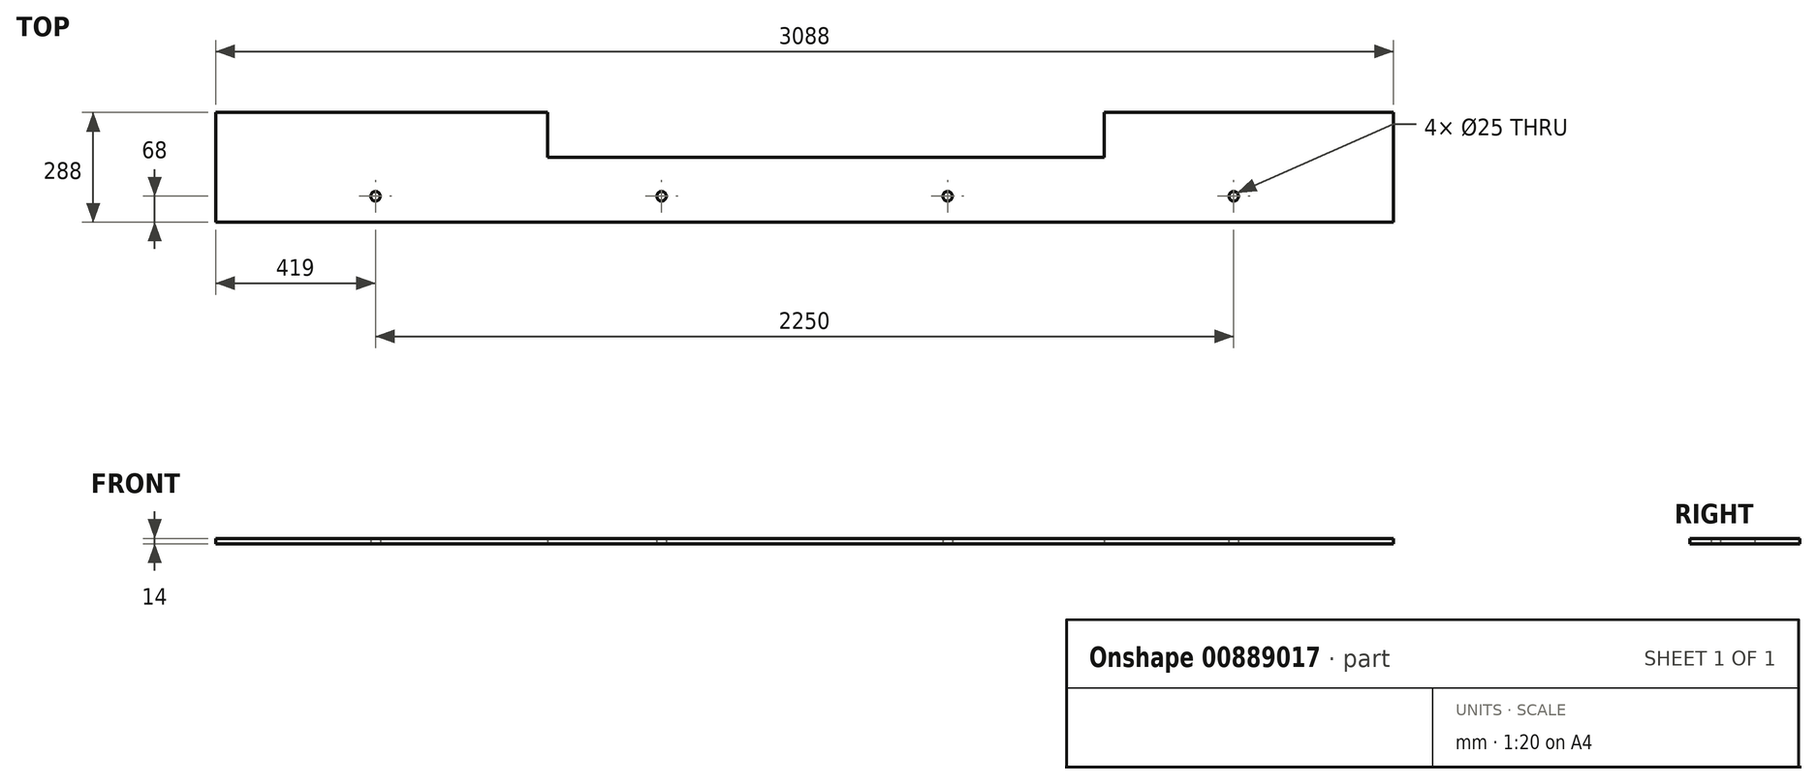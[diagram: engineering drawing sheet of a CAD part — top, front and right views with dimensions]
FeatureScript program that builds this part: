
annotation { "Feature Type Name" : "Feature", "Feature Type Description" : "" }
export const myFeature = defineFeature(function(context is Context, id is Id, definition is map)
    precondition{}
    {
        {
            var Q0;
            Q0=qCreatedBy(makeId("Top.planeOp"),FACE);
            var sketch = newSketch(context, id + "F0", { "sketchPlane" : qUnion([Q0])});
            skLineSegment(sketch, "E0.bottom", {"start": v(-1544, 144) * mm, "end": v(1544, 144) * mm});
            skLineSegment(sketch, "E0.top", {"start": v(-1544, -144) * mm, "end": v(1544, -144) * mm});
            skLineSegment(sketch, "E0.left", {"start": v(-1544, 144) * mm, "end": v(-1544, -144) * mm});
            skLineSegment(sketch, "E0.right", {"start": v(1544, 144) * mm, "end": v(1544, -144) * mm});
            skPoint(sketch, "E0.middle", {"position": v(0, 0) * mm});
            skSolve(sketch);
        }
        {
            var Q0;
            Q0=qSketchRegion(id+"F0",true);
            extrude(context, id + "F1", {"entities" : qUnion([Q0]), "depth" : 14 * mm, "offsetDistance" : 25 * mm});
        }
        {
            var Q0;
            Q0=makeQuery(id+"F1.opExtrude","CAP_FACE",FACE,{"disambiguationData":[OSD([sQuery(id+"F0.wireOp",EDGE,"E0.bottom"),sQuery(id+"F0.wireOp",EDGE,"E0.top"),sQuery(id+"F0.wireOp",EDGE,"E0.left"),sQuery(id+"F0.wireOp",EDGE,"E0.right")])],"isStart":true});
            var sketch = newSketch(context, id + "F2", { "sketchPlane" : qUnion([Q0])});
            skLineSegment(sketch, "E1.bottom", {"start": v(-674, -144) * mm, "end": v(786, -144) * mm});
            skLineSegment(sketch, "E1.top", {"start": v(-674, -26) * mm, "end": v(786, -26) * mm});
            skLineSegment(sketch, "E1.left", {"start": v(-674, -144) * mm, "end": v(-674, -26) * mm});
            skLineSegment(sketch, "E1.right", {"start": v(786, -144) * mm, "end": v(786, -26) * mm});
            skSolve(sketch);
        }
        {
            var Q0;
            Q0 = qSketchRegion(id + "F2", true);
            extrude(context, id + "F3", {"entities" : qUnion([Q0]), "operationType" : NewBodyOperationType.REMOVE, "endBound" : BoundingType.THROUGH_ALL, "oppositeDirection" : true, "depth" : 25 * mm, "offsetDistance" : 25 * mm});
        }
        {
            var Q0;
            Q0=makeQuery(id+"F1.opExtrude","CAP_FACE",FACE,{"disambiguationData":[OSD([sQuery(id+"F0.wireOp",EDGE,"E0.bottom"),sQuery(id+"F0.wireOp",EDGE,"E0.top"),sQuery(id+"F0.wireOp",EDGE,"E0.left"),sQuery(id+"F0.wireOp",EDGE,"E0.right")])],"isStart":true});
            var sketch = newSketch(context, id + "F4", { "sketchPlane" : qUnion([Q0])});
            skCircle(sketch, "E2", {"center": v(-1125, 76) * mm, "radius": 12.5 * mm});
            skCircle(sketch, "E3.1.0.0", {"center": v(-375, 76) * mm, "radius": 12.5 * mm});
            skCircle(sketch, "E3.2.0.0", {"center": v(375, 76) * mm, "radius": 12.5 * mm});
            skCircle(sketch, "E3.3.0.0", {"center": v(1125, 76) * mm, "radius": 12.5 * mm});
            skLineSegment(sketch, "E3.direction1", {"start": v(-1125, 76) * mm, "end": v(-375, 76) * mm, "construction": true});
            skSolve(sketch);
        }
        {
            var Q0;
            Q0 = qSketchRegion(id + "F4", true);
            extrude(context, id + "F5", {"entities" : qUnion([Q0]), "operationType" : NewBodyOperationType.REMOVE, "oppositeDirection" : true, "depth" : 25 * mm, "offsetDistance" : 25 * mm});
        }
    });
